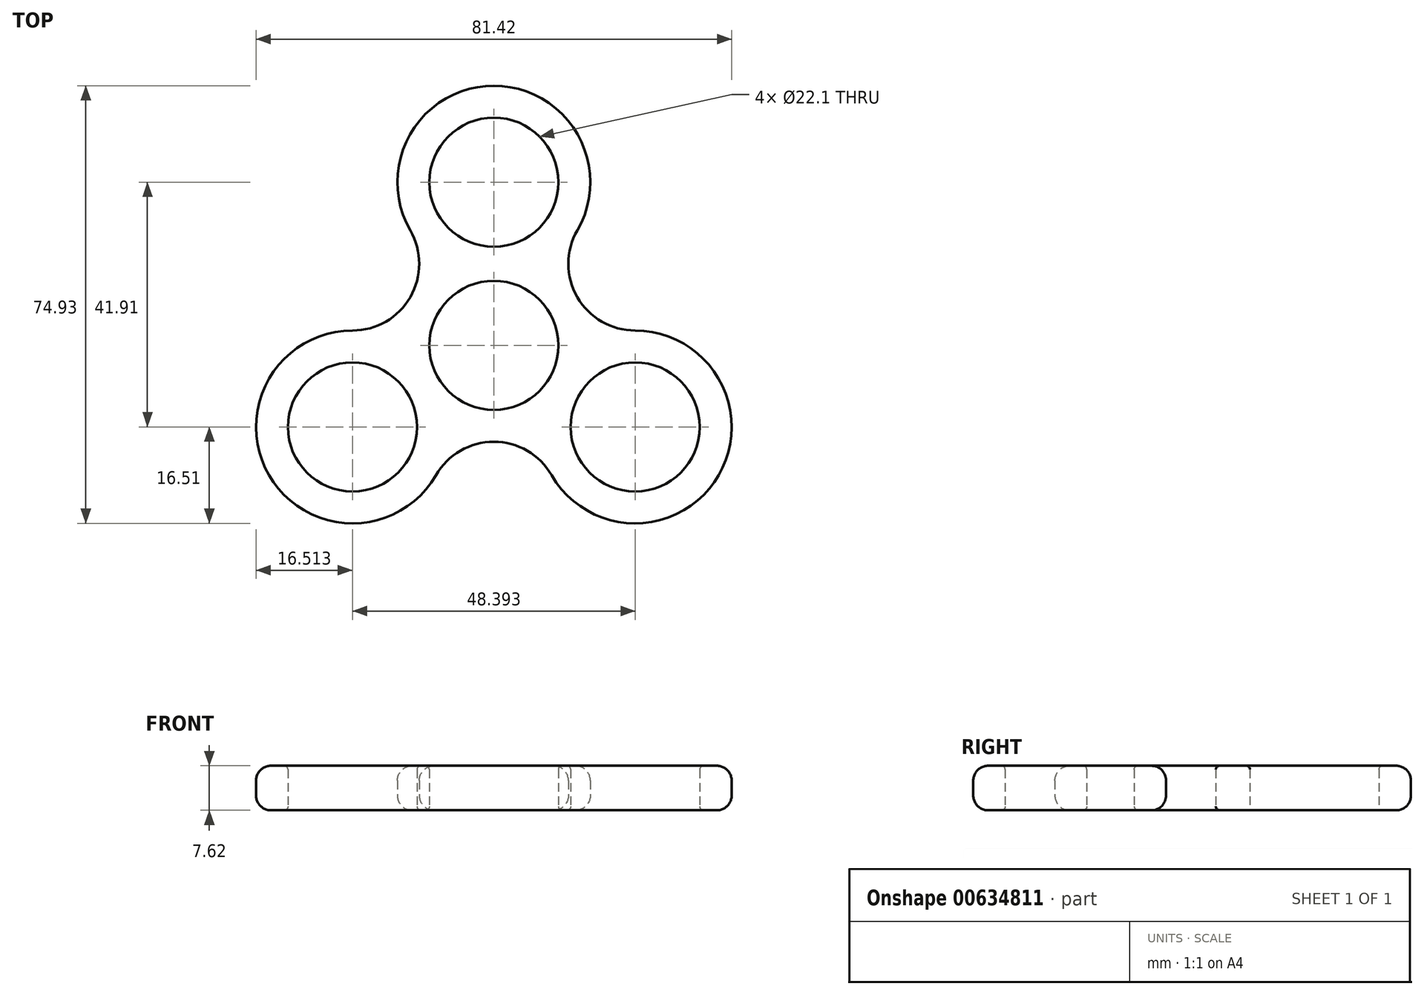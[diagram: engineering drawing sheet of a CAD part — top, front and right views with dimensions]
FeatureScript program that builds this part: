
annotation { "Feature Type Name" : "Feature", "Feature Type Description" : "" }
export const myFeature = defineFeature(function(context is Context, id is Id, definition is map)
    precondition{}
    {
        {
            var Q0;
            Q0=qCreatedBy(makeId("Top.planeOp"),FACE);
            var sketch = newSketch(context, id + "F0", { "sketchPlane" : qUnion([Q0])});
            skCircle(sketch, "E0", {"center": v(0, 0) * mm, "radius": 11.05 * mm});
            skLineSegment(sketch, "E1", {"start": v(0, 0) * mm, "end": v(0, 27.94) * mm});
            skCircle(sketch, "E2", {"center": v(0, 27.94) * mm, "radius": 11.05 * mm});
            skCircle(sketch, "E3.1.0", {"center": v(-24.2, -13.97) * mm, "radius": 11.05 * mm});
            skCircle(sketch, "E3.2.0", {"center": v(24.2, -13.97) * mm, "radius": 11.05 * mm});
            skArc(sketch, "E4", {"start": v(14.3, 19.69) * mm, "mid": v(0, 44.45) * mm, "end": v(-14.3, 19.69) * mm});
            skArc(sketch, "E5.1.0", {"start": v(-24.2, 2.54) * mm, "mid": v(-38.5, -22.22) * mm, "end": v(-9.9, -22.23) * mm});
            skArc(sketch, "E5.2.0", {"start": v(9.9, -22.23) * mm, "mid": v(38.5, -22.23) * mm, "end": v(24.2, 2.54) * mm});
            skLineSegment(sketch, "E6", {"start": v(0, 0) * mm, "end": v(-24.2, 13.97) * mm});
            skArc(sketch, "E7", {"start": v(-24.2, 2.54) * mm, "mid": v(-14.3, 8.26) * mm, "end": v(-14.3, 19.69) * mm});
            skArc(sketch, "E8.1.0", {"start": v(9.9, -22.23) * mm, "mid": v(0, -16.51) * mm, "end": v(-9.9, -22.23) * mm});
            skArc(sketch, "E8.2.0", {"start": v(14.3, 19.68) * mm, "mid": v(14.3, 8.25) * mm, "end": v(24.2, 2.54) * mm});
            skSolve(sketch);
        }
        {
            var Q0;
            Q0 = qSketchRegion(id + "F0", true);
            extrude(context, id + "F1", {"entities" : qUnion([Q0]), "depth" : 7.62 * mm, "offsetDistance" : 25.4 * mm});
        }
        {
            var Q0;
            Q0=makeQuery(id+"F1.opExtrude","CAP_EDGE",EDGE,{"disambiguationData":[OSD([sQuery(id+"F0.wireOp",EDGE,"E0")])],"isStart":false});
            var Q1;
            Q1=makeQuery(id+"F1.opExtrude","CAP_EDGE",EDGE,{"disambiguationData":[OSD([sQuery(id+"F0.wireOp",EDGE,"E0")])],"isStart":true});
            var Q2;
            Q2=makeQuery(id+"F1.opExtrude","CAP_EDGE",EDGE,{"disambiguationData":[OSD([sQuery(id+"F0.wireOp",EDGE,"E3.2.0")])],"isStart":true});
            var Q3;
            Q3=makeQuery(id+"F1.opExtrude","CAP_EDGE",EDGE,{"disambiguationData":[OSD([sQuery(id+"F0.wireOp",EDGE,"E3.1.0")])],"isStart":true});
            var Q4;
            Q4=makeQuery(id+"F1.opExtrude","CAP_EDGE",EDGE,{"disambiguationData":[OSD([sQuery(id+"F0.wireOp",EDGE,"E3.1.0")])],"isStart":false});
            var Q5;
            Q5=makeQuery(id+"F1.opExtrude","CAP_EDGE",EDGE,{"disambiguationData":[OSD([sQuery(id+"F0.wireOp",EDGE,"E3.2.0")])],"isStart":false});
            var Q6;
            Q6=makeQuery(id+"F1.opExtrude","CAP_EDGE",EDGE,{"disambiguationData":[OSD([sQuery(id+"F0.wireOp",EDGE,"E2")])],"isStart":false});
            fillet(context, id + "F2", {"entities" : qUnion([Q0, Q1, Q2, Q3, Q4, Q5, Q6]), "radius" : 0.64 * mm, "tangentPropagation" : true, "allowEdgeOverflow" : false});
        }
        {
            var Q0;
            Q0=makeQuery(id+"F1.opExtrude","CAP_EDGE",EDGE,{"disambiguationData":[OSD([sQuery(id+"F0.wireOp",EDGE,"E5.1.0")])],"isStart":false});
            var Q1;
            Q1=makeQuery(id+"F1.opExtrude","CAP_EDGE",EDGE,{"disambiguationData":[OSD([sQuery(id+"F0.wireOp",EDGE,"E5.1.0")])],"isStart":true});
            fillet(context, id + "F3", {"entities" : qUnion([Q0, Q1]), "radius" : 2.54 * mm, "tangentPropagation" : true, "allowEdgeOverflow" : false});
        }
    });
